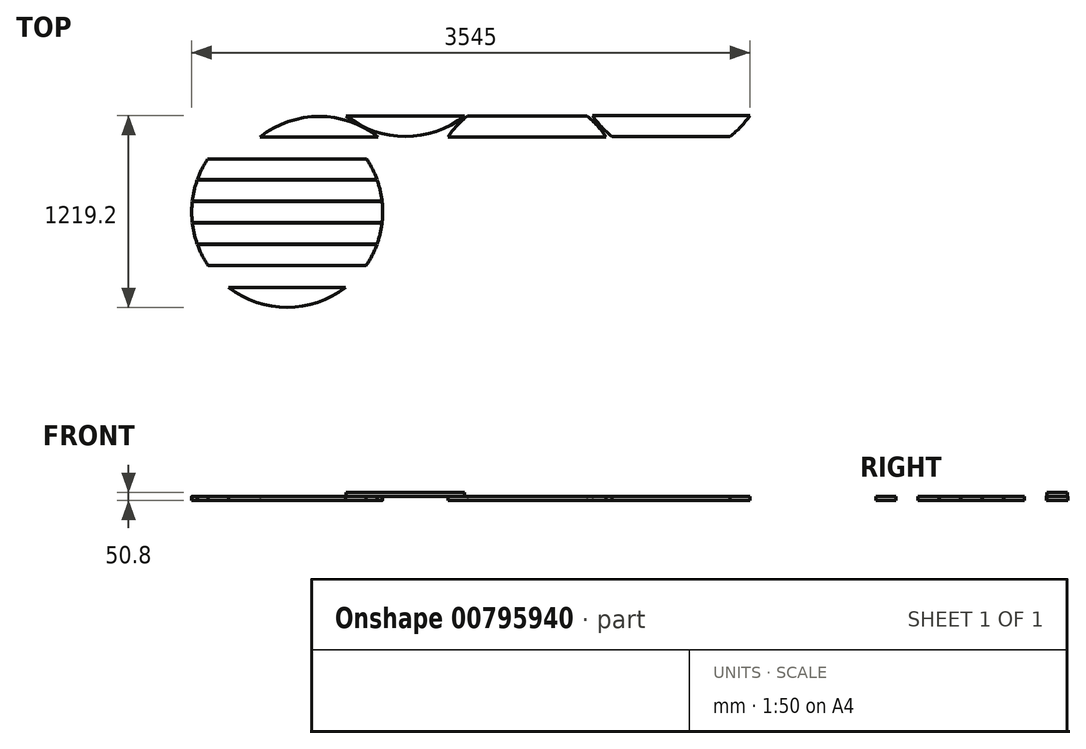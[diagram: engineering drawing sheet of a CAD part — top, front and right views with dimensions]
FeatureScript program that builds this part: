
annotation { "Feature Type Name" : "Feature", "Feature Type Description" : "" }
export const myFeature = defineFeature(function(context is Context, id is Id, definition is map)
    precondition{}
    {
        {
            var Q0;
            Q0=qCreatedBy(makeId("Top.planeOp"),FACE);
            var sketch = newSketch(context, id + "F0", { "sketchPlane" : qUnion([Q0])});
            skLineSegment(sketch, "E0.bottom", {"start": v(-602.75, 66.68) * mm, "end": v(602.75, 66.68) * mm});
            skLineSegment(sketch, "E0.top", {"start": v(-602.75, -66.68) * mm, "end": v(602.75, -66.68) * mm});
            skPoint(sketch, "E0.middle", {"position": v(0, 0) * mm});
            skLineSegment(sketch, "E1.0", {"start": v(-602.39, -69.85) * mm, "end": v(602.39, -69.85) * mm});
            skLineSegment(sketch, "E2.0", {"start": v(-571.37, -203.2) * mm, "end": v(571.37, -203.2) * mm});
            skLineSegment(sketch, "E3.0", {"start": v(-570.23, -206.38) * mm, "end": v(570.23, -206.38) * mm});
            skLineSegment(sketch, "E4.0", {"start": v(-502.33, -339.73) * mm, "end": v(502.33, -339.73) * mm});
            skLineSegment(sketch, "E5.0", {"start": v(-500.17, -342.9) * mm, "end": v(500.17, -342.9) * mm});
            skLineSegment(sketch, "E6.0", {"start": v(-375.42, -476.25) * mm, "end": v(375.42, -476.25) * mm});
            skLineSegment(sketch, "E7.0", {"start": v(-371.35, -479.43) * mm, "end": v(371.35, -479.43) * mm});
            skLineSegment(sketch, "E8.0", {"start": v(-602.39, 69.85) * mm, "end": v(602.39, 69.85) * mm});
            skLineSegment(sketch, "E9.0", {"start": v(-571.37, 203.2) * mm, "end": v(571.37, 203.2) * mm});
            skLineSegment(sketch, "E10.0", {"start": v(-570.23, 206.38) * mm, "end": v(570.23, 206.38) * mm});
            skLineSegment(sketch, "E11.0", {"start": v(-502.33, 339.73) * mm, "end": v(502.33, 339.73) * mm});
            skLineSegment(sketch, "E12.0", {"start": v(-504.47, 336.55) * mm, "end": v(504.47, 336.55) * mm});
            skLineSegment(sketch, "E13.0", {"start": v(-379.4, 473.08) * mm, "end": v(379.4, 473.08) * mm});
            skLineSegment(sketch, "E14.0", {"start": v(-375.42, 476.25) * mm, "end": v(375.42, 476.25) * mm});
            skCircle(sketch, "E15", {"center": v(0, 0) * mm, "radius": 606.43 * mm});
            skPoint(sketch, "E16.orphan", {"position": v(609.6, 66.68) * mm});
            skPoint(sketch, "E0.left.start.orphan", {"position": v(-609.6, 66.68) * mm});
            skPoint(sketch, "E17.orphan", {"position": v(-609.6, -66.68) * mm});
            skPoint(sketch, "E18.orphan", {"position": v(609.6, -66.68) * mm});
            skSolve(sketch);
        }
        {
            var Q0;
            {var subQ0=sQuery(id+"F0.wireOp",EDGE,"E14.0");Q0=makeQuery(id+"F0.imprint","IMPRINT",FACE,{"disambiguationData":[TD([[makeQuery(id+"F0.imprint","IMPRINT",EDGE,{"derivedFrom":subQ0}),1.0]])]});}
            var Q1;
            {var subQ0=sQuery(id+"F0.wireOp",EDGE,"E11.0");Q1=makeQuery(id+"F0.imprint","IMPRINT",FACE,{"disambiguationData":[TD([[makeQuery(id+"F0.imprint","IMPRINT",EDGE,{"derivedFrom":subQ0}),1.0]])]});}
            var Q2;
            {var subQ0=sQuery(id+"F0.wireOp",EDGE,"E10.0");Q2=makeQuery(id+"F0.imprint","IMPRINT",FACE,{"disambiguationData":[TD([[makeQuery(id+"F0.imprint","IMPRINT",EDGE,{"derivedFrom":subQ0}),1.0]])]});}
            var Q3;
            {var subQ0=sQuery(id+"F0.wireOp",EDGE,"E8.0");Q3=makeQuery(id+"F0.imprint","IMPRINT",FACE,{"disambiguationData":[TD([[makeQuery(id+"F0.imprint","IMPRINT",EDGE,{"derivedFrom":subQ0}),1.0]])]});}
            var Q4;
            {var subQ0=sQuery(id+"F0.wireOp",EDGE,"E0.bottom");Q4=makeQuery(id+"F0.imprint","IMPRINT",FACE,{"disambiguationData":[TD([[makeQuery(id+"F0.imprint","IMPRINT",EDGE,{"derivedFrom":subQ0}),-1.0]])]});}
            var Q5;
            {var subQ0=sQuery(id+"F0.wireOp",EDGE,"E1.0");Q5=makeQuery(id+"F0.imprint","IMPRINT",FACE,{"disambiguationData":[TD([[makeQuery(id+"F0.imprint","IMPRINT",EDGE,{"derivedFrom":subQ0}),-1.0]])]});}
            var Q6;
            {var subQ0=sQuery(id+"F0.wireOp",EDGE,"E3.0");Q6=makeQuery(id+"F0.imprint","IMPRINT",FACE,{"disambiguationData":[TD([[makeQuery(id+"F0.imprint","IMPRINT",EDGE,{"derivedFrom":subQ0}),-1.0]])]});}
            var Q7;
            {var subQ0=sQuery(id+"F0.wireOp",EDGE,"E5.0");Q7=makeQuery(id+"F0.imprint","IMPRINT",FACE,{"disambiguationData":[TD([[makeQuery(id+"F0.imprint","IMPRINT",EDGE,{"derivedFrom":subQ0}),-1.0]])]});}
            var Q8;
            {var subQ0=sQuery(id+"F0.wireOp",EDGE,"E7.0");Q8=makeQuery(id+"F0.imprint","IMPRINT",FACE,{"disambiguationData":[TD([[makeQuery(id+"F0.imprint","IMPRINT",EDGE,{"derivedFrom":subQ0}),-1.0]])]});}
            extrude(context, id + "F1", {"entities" : qUnion([Q0, Q1, Q2, Q3, Q4, Q5, Q6, Q7, Q8]), "depth" : 25.4 * mm, "offsetDistance" : 25.4 * mm});
        }
        {
            var Q0;
            Q0=makeQuery(id+"F1.opExtrude","SWEPT_BODY",BODY,{"disambiguationData":[OSD([sQuery(id+"F0.wireOp",EDGE,"E14.0"),sQuery(id+"F0.wireOp",EDGE,"E15")])]});
            var Q1;
            Q1=makeQuery(id+"F1.opExtrude","CAP_EDGE",EDGE,{"disambiguationData":[OSD([sQuery(id+"F0.wireOp",EDGE,"E14.0")])],"isStart":false});
            transform(context, id + "F2", {"entities" : qUnion([Q0]), "transformType" : TransformType.ROTATION, "transformAxis" : qUnion([Q1]), "angle" : 180 * degree, "makeCopy" : true});
        }
        {
            var Q0;
            Q0=makeQuery(id+"F2.opPattern","COPY",BODY,{"derivedFrom":makeQuery(id+"F1.opExtrude","SWEPT_BODY",BODY,{"disambiguationData":[OSD([sQuery(id+"F0.wireOp",EDGE,"E14.0"),sQuery(id+"F0.wireOp",EDGE,"E15")])]}),"instanceName":"1"});
            var Q1;
            Q1=makeQuery(id+"F2.opPattern","COPY",EDGE,{"derivedFrom":makeQuery(id+"F1.opExtrude","CAP_EDGE",EDGE,{"disambiguationData":[OSD([sQuery(id+"F0.wireOp",EDGE,"E14.0")])],"isStart":true}),"instanceName":"1"});
            transform(context, id + "F3", {"entities" : qUnion([Q0]), "transformType" : TransformType.TRANSLATION_ENTITY, "oppositeDirectionEntity" : false, "transformLine" : qUnion([Q1]), "makeCopy" : false});
        }
        {
            var Q0;
            Q0=makeQuery(id+"F2.opPattern","COPY",BODY,{"derivedFrom":makeQuery(id+"F1.opExtrude","SWEPT_BODY",BODY,{"disambiguationData":[OSD([sQuery(id+"F0.wireOp",EDGE,"E14.0"),sQuery(id+"F0.wireOp",EDGE,"E15")])]}),"instanceName":"1"});
            var Q1;
            Q1=makeQuery(id+"F2.opPattern","COPY",FACE,{"derivedFrom":makeQuery(id+"F1.opExtrude","SWEPT_FACE",FACE,{"disambiguationData":[OSD([sQuery(id+"F0.wireOp",EDGE,"E14.0")])]}),"instanceName":"1"});
            var Q2;
            Q2=makeQuery(id+"F2.opPattern","COPY",FACE,{"derivedFrom":makeQuery(id+"F1.opExtrude","CAP_FACE",FACE,{"disambiguationData":[OSD([sQuery(id+"F0.wireOp",EDGE,"E14.0"),sQuery(id+"F0.wireOp",EDGE,"E15")])],"isStart":true}),"instanceName":"1"});
            transform(context, id + "F4", {"entities" : qUnion([Q0]), "transformType" : TransformType.TRANSLATION_DISTANCE, "transformDirection" : qUnion([Q1, Q2]), "distance" : 133.35 * mm, "makeCopy" : false});
        }
        {
            var Q0;
            Q0=makeQuery(id+"F1.opExtrude","SWEPT_BODY",BODY,{"disambiguationData":[OSD([sQuery(id+"F0.wireOp",EDGE,"E14.0"),sQuery(id+"F0.wireOp",EDGE,"E15")])]});
            transform(context, id + "F5", {"entities" : qUnion([Q0]), "transformType" : TransformType.TRANSLATION_3D, "dx" : 203.2 * mm, "dy" : 0 * mm, "dz" : 0 * mm, "makeCopy" : false});
        }
        {
            var Q0;
            Q0=makeQuery(id+"F1.opExtrude","SWEPT_BODY",BODY,{"disambiguationData":[OSD([sQuery(id+"F0.wireOp",EDGE,"E11.0"),sQuery(id+"F0.wireOp",EDGE,"E13.0"),sQuery(id+"F0.wireOp",EDGE,"E15")])]});
            transform(context, id + "F6", {"entities" : qUnion([Q0]), "transformType" : TransformType.TRANSLATION_3D, "dx" : 1524 * mm, "dy" : 136.53 * mm, "dz" : 0 * mm, "makeCopy" : false});
        }
        {
            var Q0;
            Q0=makeQuery(id+"F1.opExtrude","SWEPT_BODY",BODY,{"disambiguationData":[OSD([sQuery(id+"F0.wireOp",EDGE,"E5.0"),sQuery(id+"F0.wireOp",EDGE,"E6.0"),sQuery(id+"F0.wireOp",EDGE,"E15")])]});
            transform(context, id + "F7", {"entities" : qUnion([Q0]), "transformType" : TransformType.TRANSLATION_3D, "dx" : 2438.4 * mm, "dy" : 955.67 * mm, "dz" : 0 * mm, "makeCopy" : false});
        }
    });
